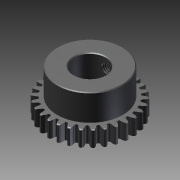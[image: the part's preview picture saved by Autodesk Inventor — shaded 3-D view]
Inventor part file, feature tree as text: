
AUTODESK INVENTOR PART (.ipt)
format: ipt  version: 2011 SP1 (Build 150282100, 282)  size: 964,608 bytes
history: native  units: mm
features: other x21, revolve x4, sketch x4, extrude x1, hole x1, thread x1
ambient origin geometry x8: Origin, YZ Plane, XZ Plane, XY Plane, X Axis, Y Axis, Z Axis, Center Point
bodies: Solid1 (feature_tree)
feature tree (32):
  revolve  "Revolution1"  [1 undecoded]
  extrude  "Extrusion1"  TaperAngle=360.0deg  [1 undecoded]
  hole  "Hole1"  [1 undecoded]
  revolve  "Revolution2"  [1 undecoded]
  revolve  "Revolution3"  [1 undecoded]
  revolve  "Revolution4"  [1 undecoded]
  thread  "Thread1"  [1 undecoded]
  other  "b_XY"
  other  "b_YZ"
  other  "b_ZX"
  other  "b_X"
  other  "b_Y"
  other  "b_Z"
  other  "b_Center"
  other  "screw_XY"
  other  "screw_YZ"
  other  "screw_ZX"
  other  "screw_X"
  other  "screw_Y"
  other  "screw_Z"
  other  "screw_Center"
  other  "turn_around_XY"
  other  "turn_around_YZ"
  other  "turn_around_ZX"
  other  "turn_around_X"
  other  "turn_around_Y"
  other  "turn_around_Z"
  other  "turn_around_Center"
  sketch  "Sketch_2"  dims[d0=360.0deg d1=6.0mm d2=0.0mm]
  sketch  "Sketch_3"  dims[d3=12.0mm d4=6.0mm d5=4.0mm d6=2.0mm d7=90.0deg d8=16.0mm d9=0.0mm d10=360.0deg]
  sketch  "Sketch3"  dims[d11=360.0deg d12=360.0deg]
  sketch  "Sketch_4"  dims[d13=6.121mm d14=0.0mm d15=0.0mm]
note: 7 required parameter values undecoded (feature->parameter linkage not recoverable at this tier; creation-order binding heuristic only, values carry confidence <= 0.55)